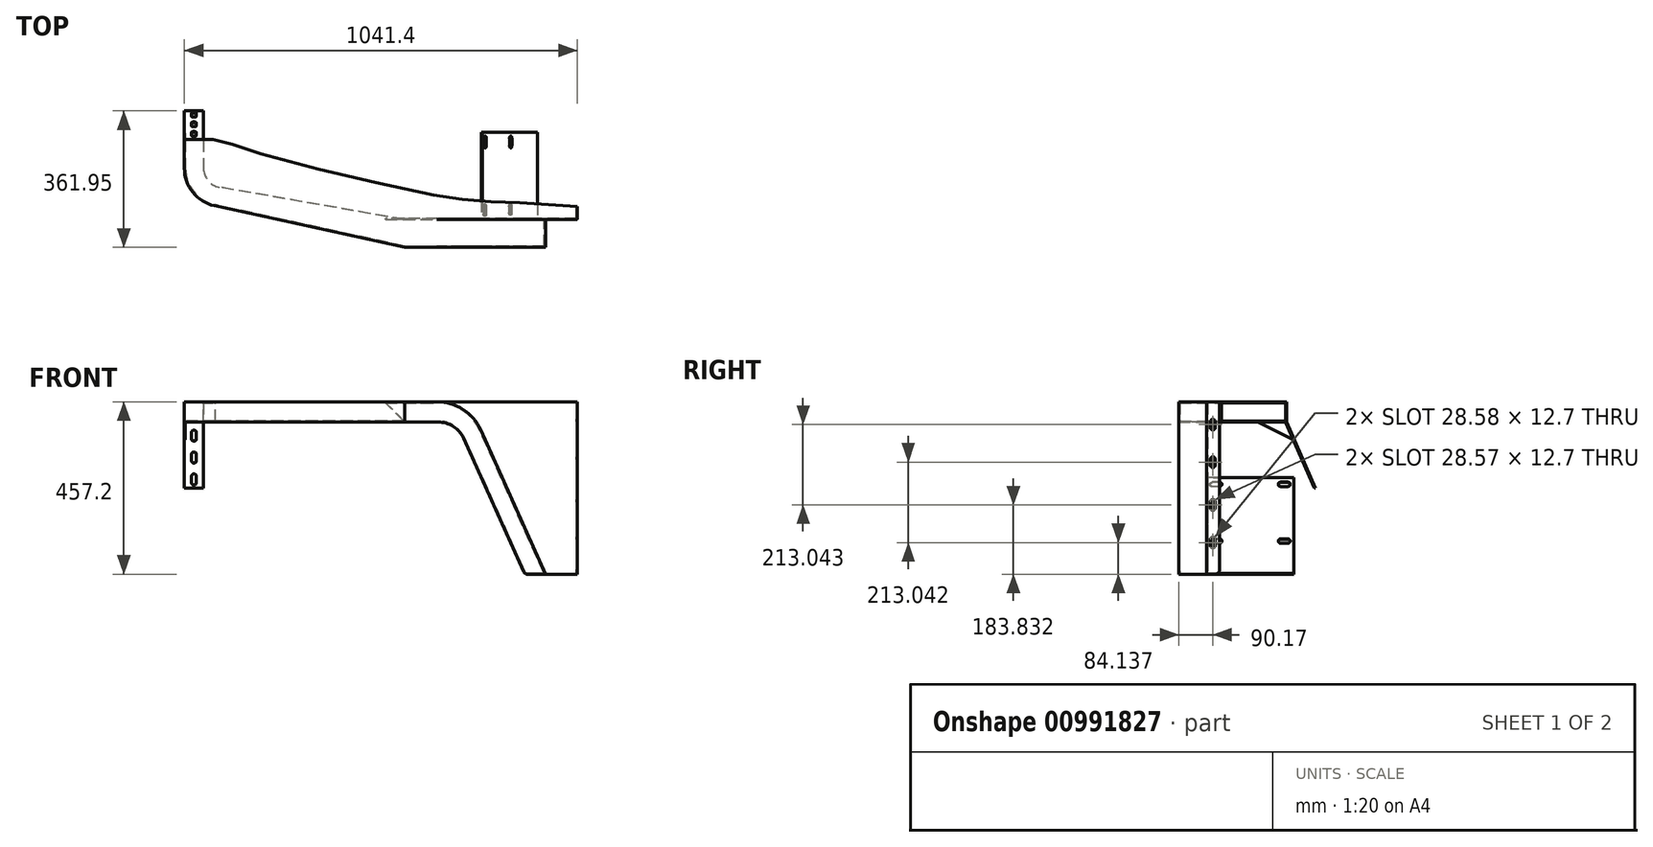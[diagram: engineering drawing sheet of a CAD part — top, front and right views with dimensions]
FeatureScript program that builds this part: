
annotation { "Feature Type Name" : "Feature", "Feature Type Description" : "" }
export const myFeature = defineFeature(function(context is Context, id is Id, definition is map)
    precondition{}
    {
        {
            var Q0;
            Q0=qCreatedBy(makeId("Top.planeOp"),FACE);
            var sketch = newSketch(context, id + "F0", { "sketchPlane" : qUnion([Q0])});
            skLineSegment(sketch, "E0", {"start": v(-1041.4, 177.8) * mm, "end": v(-965.2, 177.8) * mm});
            skLineSegment(sketch, "E1", {"start": v(0, 0) * mm, "end": v(-76.2, 5.08) * mm});
            skLineSegment(sketch, "E2", {"start": v(-76.2, 5.08) * mm, "end": v(-152.4, 10.16) * mm});
            skLineSegment(sketch, "E3", {"start": v(-152.4, 10.16) * mm, "end": v(-228.6, 12.7) * mm});
            skLineSegment(sketch, "E4", {"start": v(-228.6, 12.7) * mm, "end": v(-304.8, 19.05) * mm});
            skLineSegment(sketch, "E5", {"start": v(-304.8, 19.05) * mm, "end": v(-381, 30.48) * mm});
            skLineSegment(sketch, "E6", {"start": v(-381, 30.48) * mm, "end": v(-457.2, 46.99) * mm});
            skLineSegment(sketch, "E7", {"start": v(-457.2, 46.99) * mm, "end": v(-533.4, 63.5) * mm});
            skLineSegment(sketch, "E8", {"start": v(-533.4, 63.5) * mm, "end": v(-609.6, 81.73) * mm});
            skLineSegment(sketch, "E9", {"start": v(-609.6, 81.73) * mm, "end": v(-685.8, 99.57) * mm});
            skLineSegment(sketch, "E10", {"start": v(-685.8, 99.57) * mm, "end": v(-762, 119.38) * mm});
            skLineSegment(sketch, "E11", {"start": v(-762, 119.38) * mm, "end": v(-838.2, 139.7) * mm});
            skLineSegment(sketch, "E12", {"start": v(-838.2, 139.7) * mm, "end": v(-914.4, 165.1) * mm});
            skLineSegment(sketch, "E13", {"start": v(-914.4, 165.1) * mm, "end": v(-965.2, 177.8) * mm});
            skLineSegment(sketch, "E14", {"start": v(0, 0) * mm, "end": v(0, -31.75) * mm});
            skLineSegment(sketch, "E15", {"start": v(-1041.4, 177.8) * mm, "end": v(-1041.4, 101.6) * mm});
            skArc(sketch, "E16", {"start": v(-1041.4, 101.6) * mm, "mid": v(-1018.95, 37.9) * mm, "end": v(-961.5, 2.35) * mm});
            skLineSegment(sketch, "E17", {"start": v(0, -31.75) * mm, "end": v(-457.2, -31.75) * mm});
            skLineSegment(sketch, "E18", {"start": v(-457.2, -31.75) * mm, "end": v(-457.2, -107.95) * mm});
            skLineSegment(sketch, "E19", {"start": v(-961.5, 2.35) * mm, "end": v(-457.2, -107.95) * mm});
            skSolve(sketch);
        }
        {
            var Q0;
            Q0 = qSketchRegion(id + "F0", true);
            extrude(context, id + "F1", {"entities" : qUnion([Q0]), "oppositeDirection" : true, "depth" : 2.8 * mm, "offsetDistance" : 25.4 * mm});
        }
        {
            var Q0;
            Q0=makeQuery(id+"F1.opExtrude","SWEPT_FACE",FACE,{"disambiguationData":[OSD([sQuery(id+"F0.wireOp",EDGE,"E15")])]});
            var sketch = newSketch(context, id + "F2", { "sketchPlane" : qUnion([Q0])});
            skLineSegment(sketch, "E20", {"start": v(-177.8, -2.8) * mm, "end": v(-177.8, -53.33) * mm});
            skLineSegment(sketch, "E21", {"start": v(-177.9, -53.84) * mm, "end": v(-254, -228.2) * mm});
            skLineSegment(sketch, "E22", {"start": v(-254, -228.2) * mm, "end": v(-251.44, -229.3) * mm});
            skLineSegment(sketch, "E23", {"start": v(-251.44, -229.3) * mm, "end": v(-175.11, -54.42) * mm});
            skLineSegment(sketch, "E24", {"start": v(-175, -53.91) * mm, "end": v(-175, -2.8) * mm});
            skPoint(sketch, "E24.endSnap0", {"position": v(-139.7, -2.8) * mm});
            skLineSegment(sketch, "E25", {"start": v(-175, -2.8) * mm, "end": v(-177.8, -2.8) * mm});
            skPoint(sketch, "E26.visualSharp", {"position": v(-177.8, -53.6) * mm});
            skArc(sketch, "E26.filletArc", {"start": v(-177.9, -53.84) * mm, "mid": v(-177.83, -53.59) * mm, "end": v(-177.8, -53.33) * mm});
            skPoint(sketch, "E27.visualSharp", {"position": v(-175, -54.18) * mm});
            skArc(sketch, "E27.filletArc", {"start": v(-175.11, -54.42) * mm, "mid": v(-175.03, -54.17) * mm, "end": v(-175, -53.91) * mm});
            skSolve(sketch);
        }
        {
            var Q0;
            Q0 = qSketchRegion(id + "F2", true);
            extrude(context, id + "F3", {"entities" : qUnion([Q0]), "operationType" : NewBodyOperationType.ADD, "oppositeDirection" : true, "depth" : 50.8 * mm, "offsetDistance" : 25.4 * mm});
        }
        {
            var Q0;
            Q0=makeQuery(id+"F3.opExtrude","SWEPT_FACE",FACE,{"disambiguationData":[OSD([sQuery(id+"F2.wireOp",EDGE,"E21")])]});
            var sketch = newSketch(context, id + "F4", { "sketchPlane" : qUnion([Q0])});
            skArc(sketch, "E28", {"start": v(1022.34, -149.13) * mm, "mid": v(1015.88, -142.47) * mm, "end": v(1009.67, -149.36) * mm});
            skArc(sketch, "E29", {"start": v(1009.67, -167.32) * mm, "mid": v(1015.73, -174.2) * mm, "end": v(1022.35, -167.86) * mm});
            skArc(sketch, "E30", {"start": v(1022.35, -212) * mm, "mid": v(1016, -205.65) * mm, "end": v(1009.65, -212) * mm});
            skArc(sketch, "E31", {"start": v(1009.65, -231.36) * mm, "mid": v(1016, -237.71) * mm, "end": v(1022.35, -231.36) * mm});
            skArc(sketch, "E32", {"start": v(1022.35, -275.5) * mm, "mid": v(1015.84, -269.15) * mm, "end": v(1009.66, -275.81) * mm});
            skArc(sketch, "E33", {"start": v(1009.65, -294.86) * mm, "mid": v(1016, -301.21) * mm, "end": v(1022.35, -294.86) * mm});
            skLineSegment(sketch, "E34", {"start": v(1009.67, -148.27) * mm, "end": v(1009.67, -168.41) * mm});
            skLineSegment(sketch, "E35", {"start": v(1022.34, -148.5) * mm, "end": v(1022.35, -167.86) * mm});
            skLineSegment(sketch, "E36", {"start": v(1009.65, -212) * mm, "end": v(1009.65, -231.36) * mm});
            skLineSegment(sketch, "E37", {"start": v(1022.35, -212) * mm, "end": v(1022.35, -231.36) * mm});
            skLineSegment(sketch, "E38", {"start": v(1022.35, -275.5) * mm, "end": v(1022.35, -294.86) * mm});
            skLineSegment(sketch, "E39", {"start": v(1009.66, -275.81) * mm, "end": v(1009.65, -294.86) * mm});
            skSolve(sketch);
        }
        {
            var Q0;
            Q0 = qSketchRegion(id + "F4", true);
            extrude(context, id + "F5", {"entities" : qUnion([Q0]), "operationType" : NewBodyOperationType.REMOVE, "oppositeDirection" : true, "depth" : 25.4 * mm, "offsetDistance" : 25.4 * mm});
        }
        {
            var Q0;
            Q0=makeQuery(id+"F1.opExtrude","CAP_FACE",FACE,{"disambiguationData":[OSD([sQuery(id+"F0.wireOp",EDGE,"E0"),sQuery(id+"F0.wireOp",EDGE,"E1"),sQuery(id+"F0.wireOp",EDGE,"E2"),sQuery(id+"F0.wireOp",EDGE,"E3"),sQuery(id+"F0.wireOp",EDGE,"E4"),sQuery(id+"F0.wireOp",EDGE,"E5"),sQuery(id+"F0.wireOp",EDGE,"E6"),sQuery(id+"F0.wireOp",EDGE,"E7"),sQuery(id+"F0.wireOp",EDGE,"E8"),sQuery(id+"F0.wireOp",EDGE,"E9"),sQuery(id+"F0.wireOp",EDGE,"E10"),sQuery(id+"F0.wireOp",EDGE,"E11"),sQuery(id+"F0.wireOp",EDGE,"E12"),sQuery(id+"F0.wireOp",EDGE,"E13"),sQuery(id+"F0.wireOp",EDGE,"E14"),sQuery(id+"F0.wireOp",EDGE,"E15"),sQuery(id+"F0.wireOp",EDGE,"E16"),sQuery(id+"F0.wireOp",EDGE,"E17"),sQuery(id+"F0.wireOp",EDGE,"E18"),sQuery(id+"F0.wireOp",EDGE,"E19")])],"isStart":false});
            var sketch = newSketch(context, id + "F6", { "sketchPlane" : qUnion([Q0])});
            skLineSegment(sketch, "E40", {"start": v(-1041.4, -175) * mm, "end": v(-1041.4, -101.6) * mm});
            skLineSegment(sketch, "E41", {"start": v(-1038.6, -175) * mm, "end": v(-1038.6, -101.6) * mm});
            skArc(sketch, "E42", {"start": v(-961.5, -2.35) * mm, "mid": v(-1018.95, -37.9) * mm, "end": v(-1041.4, -101.6) * mm});
            skArc(sketch, "E43", {"start": v(-959.54, -4.79) * mm, "mid": v(-1016.33, -39.1) * mm, "end": v(-1038.6, -101.6) * mm});
            skLineSegment(sketch, "E44", {"start": v(-961.5, -2.35) * mm, "end": v(-457.2, 107.95) * mm});
            skLineSegment(sketch, "E45", {"start": v(-457.2, 105.08) * mm, "end": v(-959.54, -4.79) * mm});
            skLineSegment(sketch, "E46", {"start": v(-457.2, 105.08) * mm, "end": v(-457.2, 107.95) * mm});
            skLineSegment(sketch, "E47", {"start": v(-1041.4, -175) * mm, "end": v(-1038.6, -175) * mm});
            skSolve(sketch);
        }
        {
            var Q0;
            Q0 = qSketchRegion(id + "F6", true);
            extrude(context, id + "F7", {"entities" : qUnion([Q0]), "operationType" : NewBodyOperationType.ADD, "depth" : 50.8 * mm, "offsetDistance" : 25.4 * mm});
        }
        {
            var Q0;
            Q0=makeQuery(id+"F1.opExtrude","SWEPT_FACE",FACE,{"disambiguationData":[OSD([sQuery(id+"F0.wireOp",EDGE,"E17")])]});
            var sketch = newSketch(context, id + "F8", { "sketchPlane" : qUnion([Q0])});
            skLineSegment(sketch, "E48", {"start": v(0, 0) * mm, "end": v(0, -457.2) * mm});
            skLineSegment(sketch, "E49", {"start": v(0, -457.2) * mm, "end": v(-139.7, -457.2) * mm});
            skLineSegment(sketch, "E50", {"start": v(-457.2, 0) * mm, "end": v(-406.4, 0) * mm});
            skLineSegment(sketch, "E51", {"start": v(-457.2, 0) * mm, "end": v(-457.2, -2.8) * mm});
            skLineSegment(sketch, "E52", {"start": v(-406.4, 0) * mm, "end": v(0, 0) * mm});
            skPoint(sketch, "E53.visualSharp", {"position": v(-139.7, -457.2) * mm});
            skPoint(sketch, "E54.visualSharp", {"position": v(0, -457.2) * mm});
            skLineSegment(sketch, "E55", {"start": v(-139.7, -457.2) * mm, "end": v(-254, -203.2) * mm});
            skLineSegment(sketch, "E56", {"start": v(-457.2, -53.6) * mm, "end": v(-368.79, -53.6) * mm});
            skArc(sketch, "E57", {"start": v(-301.85, -96.88) * mm, "mid": v(-328.93, -65.36) * mm, "end": v(-368.79, -53.6) * mm});
            skLineSegment(sketch, "E58", {"start": v(-254, -203.2) * mm, "end": v(-301.85, -96.88) * mm});
            skLineSegment(sketch, "E59", {"start": v(-457.2, -53.6) * mm, "end": v(-508, -2.8) * mm});
            skLineSegment(sketch, "E60", {"start": v(-508, -2.8) * mm, "end": v(-457.2, -2.8) * mm});
            skSolve(sketch);
        }
        {
            var Q0;
            Q0 = qSketchRegion(id + "F8", true);
            extrude(context, id + "F9", {"entities" : qUnion([Q0]), "operationType" : NewBodyOperationType.ADD, "depth" : 2.8 * mm, "offsetDistance" : 25.4 * mm});
        }
        {
            var Q0;
            Q0=makeQuery(id+"F7.boolean.opBoolean","MERGE",FACE,{"derivedFrom":[makeQuery(id+"F3.boolean.opBoolean","MERGE",FACE,{"derivedFrom":[makeQuery(id+"F1.opExtrude","SWEPT_FACE",FACE,{"disambiguationData":[OSD([sQuery(id+"F0.wireOp",EDGE,"E15")])]}),makeQuery(id+"F3.opExtrude","CAP_FACE",FACE,{"disambiguationData":[OSD([sQuery(id+"F2.wireOp",EDGE,"E20"),sQuery(id+"F2.wireOp",EDGE,"E21"),sQuery(id+"F2.wireOp",EDGE,"E22"),sQuery(id+"F2.wireOp",EDGE,"E23"),sQuery(id+"F2.wireOp",EDGE,"E24"),sQuery(id+"F2.wireOp",EDGE,"E25"),sQuery(id+"F2.wireOp",EDGE,"E26.filletArc"),sQuery(id+"F2.wireOp",EDGE,"E27.filletArc")])],"isStart":true})]}),makeQuery(id+"F7.opExtrude","SWEPT_FACE",FACE,{"disambiguationData":[OSD([sQuery(id+"F6.wireOp",EDGE,"E40")])]})]});
            var sketch = newSketch(context, id + "F10", { "sketchPlane" : qUnion([Q0])});
            skLineSegment(sketch, "E61", {"start": v(-101.6, -53.6) * mm, "end": v(-195.23, -100.51) * mm});
            skLineSegment(sketch, "E62", {"start": v(-195.23, -100.51) * mm, "end": v(-175, -53.91) * mm});
            skLineSegment(sketch, "E63", {"start": v(-175, -53.6) * mm, "end": v(-101.6, -53.6) * mm});
            skSolve(sketch);
        }
        {
            var Q0;
            {var subQ1=sQuery(id+"F10.wireOp",EDGE,"E61");Q0=makeQuery(id+"F10.imprint","IMPRINT",FACE,{"disambiguationData":[TD([[makeQuery(id+"F10.imprint","IMPRINT",EDGE,{"derivedFrom":subQ1}),-1.0]])]});}
            extrude(context, id + "F11", {"entities" : qUnion([Q0]), "operationType" : NewBodyOperationType.ADD, "oppositeDirection" : true, "depth" : 2.8 * mm, "offsetDistance" : 25.4 * mm});
        }
        {
            var Q0;
            Q0=makeQuery(id+"F9.opExtrude","SWEPT_EDGE",EDGE,{"disambiguationData":[OSD([sQuery(id+"F8.wireOp",EDGE,"E49"),sQuery(id+"F8.wireOp",EDGE,"E55")])]});
            fillet(context, id + "F12", {"entities" : qUnion([Q0]), "radius" : 12.7 * mm, "tangentPropagation" : true, "allowEdgeOverflow" : false});
        }
        {
            var Q0;
            Q0=makeQuery(id+"F9.opExtrude","CAP_FACE",FACE,{"disambiguationData":[OSD([sQuery(id+"F8.wireOp",EDGE,"E48"),sQuery(id+"F8.wireOp",EDGE,"E49"),sQuery(id+"F8.wireOp",EDGE,"E50"),sQuery(id+"F8.wireOp",EDGE,"E51"),sQuery(id+"F8.wireOp",EDGE,"E52"),sQuery(id+"F8.wireOp",EDGE,"E55"),sQuery(id+"F8.wireOp",EDGE,"E56"),sQuery(id+"F8.wireOp",EDGE,"E57"),sQuery(id+"F8.wireOp",EDGE,"E58"),sQuery(id+"F8.wireOp",EDGE,"E59"),sQuery(id+"F8.wireOp",EDGE,"E60")])],"isStart":false});
            var sketch = newSketch(context, id + "F13", { "sketchPlane" : qUnion([Q0])});
            skLineSegment(sketch, "E64", {"start": v(-457.2, 0) * mm, "end": v(-371.85, 0) * mm});
            skLineSegment(sketch, "E65", {"start": v(-457.2, 0) * mm, "end": v(-457.2, -2.8) * mm});
            skLineSegment(sketch, "E66", {"start": v(-457.2, -2.8) * mm, "end": v(-371.85, -2.8) * mm});
            skLineSegment(sketch, "E67", {"start": v(-84, -457.2) * mm, "end": v(-256.04, -74.88) * mm});
            skArc(sketch, "E68", {"start": v(-256.04, -74.88) * mm, "mid": v(-302.9, -20.35) * mm, "end": v(-371.85, 0) * mm});
            skArc(sketch, "E69", {"start": v(-258.58, -76.03) * mm, "mid": v(-304.4, -22.7) * mm, "end": v(-371.85, -2.8) * mm});
            skLineSegment(sketch, "E70", {"start": v(-87.06, -457.2) * mm, "end": v(-258.58, -76.03) * mm});
            skLineSegment(sketch, "E71", {"start": v(-84, -457.2) * mm, "end": v(-87.06, -457.2) * mm});
            skSolve(sketch);
        }
        {
            var Q0;
            Q0 = qSketchRegion(id + "F10", true);
            var Q1;
            Q1 = qSketchRegion(id + "F13", true);
            extrude(context, id + "F14", {"entities" : qUnion([Q0, Q1]), "operationType" : NewBodyOperationType.ADD, "depth" : 76.2 * mm - 2.8 * mm, "offsetDistance" : 25.4 * mm});
        }
        {
            var Q0;
            Q0=makeQuery(id+"F14.opExtrude","CAP_FACE",FACE,{"disambiguationData":[OSD([sQuery(id+"F13.wireOp",EDGE,"E64"),sQuery(id+"F13.wireOp",EDGE,"E65"),sQuery(id+"F13.wireOp",EDGE,"E66"),sQuery(id+"F13.wireOp",EDGE,"E67"),sQuery(id+"F13.wireOp",EDGE,"E68"),sQuery(id+"F13.wireOp",EDGE,"E69"),sQuery(id+"F13.wireOp",EDGE,"E70"),sQuery(id+"F13.wireOp",EDGE,"E71")])],"isStart":false});
            var sketch = newSketch(context, id + "F15", { "sketchPlane" : qUnion([Q0])});
            skLineSegment(sketch, "E72", {"start": v(-457.2, -2.8) * mm, "end": v(-457.2, -53.6) * mm});
            skLineSegment(sketch, "E73", {"start": v(-457.2, -2.8) * mm, "end": v(-371.85, -2.8) * mm});
            skArc(sketch, "E74", {"start": v(-258.58, -76.03) * mm, "mid": v(-304.4, -22.7) * mm, "end": v(-371.85, -2.8) * mm});
            skLineSegment(sketch, "E75", {"start": v(-87.06, -457.2) * mm, "end": v(-258.58, -76.03) * mm});
            skLineSegment(sketch, "E76", {"start": v(-457.2, -53.6) * mm, "end": v(-368.79, -53.6) * mm});
            skArc(sketch, "E77", {"start": v(-301.85, -96.88) * mm, "mid": v(-328.93, -65.36) * mm, "end": v(-368.79, -53.6) * mm});
            skLineSegment(sketch, "E78", {"start": v(-143.07, -449.71) * mm, "end": v(-301.85, -96.88) * mm});
            skLineSegment(sketch, "E79", {"start": v(-131.49, -457.2) * mm, "end": v(-87.06, -457.2) * mm});
            skPoint(sketch, "E80.visualSharp", {"position": v(-139.7, -457.2) * mm});
            skArc(sketch, "E80.filletArc", {"start": v(-143.07, -449.71) * mm, "mid": v(-138.38, -455.16) * mm, "end": v(-131.49, -457.2) * mm});
            skSolve(sketch);
        }
        {
            var Q0;
            Q0=makeQuery(id+"F15.imprint","IMPRINT",FACE,{"disambiguationData":[TD([[makeQuery(id+"F15.imprint","IMPRINT",EDGE,{"derivedFrom":sQuery(id+"F15.wireOp",EDGE,"E72")}),1.0]])]});
            extrude(context, id + "F16", {"entities" : qUnion([Q0]), "operationType" : NewBodyOperationType.ADD, "oppositeDirection" : true, "depth" : 2.8 * mm, "offsetDistance" : 25.4 * mm});
        }
        {
            var Q0;
            Q0=makeQuery(id+"F16.boolean.opBoolean","MERGE",FACE,{"derivedFrom":[makeQuery(id+"F7.opExtrude","CAP_FACE",FACE,{"disambiguationData":[OSD([sQuery(id+"F6.wireOp",EDGE,"E40"),sQuery(id+"F6.wireOp",EDGE,"E41"),sQuery(id+"F6.wireOp",EDGE,"E42"),sQuery(id+"F6.wireOp",EDGE,"E43"),sQuery(id+"F6.wireOp",EDGE,"E44"),sQuery(id+"F6.wireOp",EDGE,"E45"),sQuery(id+"F6.wireOp",EDGE,"E46"),sQuery(id+"F6.wireOp",EDGE,"E47")])],"isStart":false}),makeQuery(id+"F16.opExtrude","SWEPT_FACE",FACE,{"disambiguationData":[OSD([sQuery(id+"F15.wireOp",EDGE,"E76")])]})]});
            var sketch = newSketch(context, id + "F17", { "sketchPlane" : qUnion([Q0])});
            skLineSegment(sketch, "E81", {"start": v(-1038.6, -101.6) * mm, "end": v(-1038.6, -175) * mm});
            skArc(sketch, "E82", {"start": v(-959.54, -4.79) * mm, "mid": v(-1016.33, -39.1) * mm, "end": v(-1038.6, -101.6) * mm});
            skLineSegment(sketch, "E83", {"start": v(-419.1, 105.16) * mm, "end": v(-419.1, 34.54) * mm});
            skLineSegment(sketch, "E84", {"start": v(-419.1, 34.54) * mm, "end": v(-457.2, 34.54) * mm});
            skLineSegment(sketch, "E85", {"start": v(-1038.6, -175) * mm, "end": v(-990.6, -175) * mm});
            skLineSegment(sketch, "E86", {"start": v(-990.6, -175) * mm, "end": v(-990.6, -101.6) * mm});
            skArc(sketch, "E87", {"start": v(-948.57, -51.56) * mm, "mid": v(-978.7, -68.93) * mm, "end": v(-990.6, -101.6) * mm});
            skLineSegment(sketch, "E88", {"start": v(-457.2, 34.54) * mm, "end": v(-948.57, -51.56) * mm});
            skLineSegment(sketch, "E89", {"start": v(-419.1, 105.16) * mm, "end": v(-457.2, 105.16) * mm});
            skLineSegment(sketch, "E90", {"start": v(-457.2, 105.16) * mm, "end": v(-959.54, -4.79) * mm});
            skSolve(sketch);
        }
        {
            var Q0;
            {var subQ0=sQuery(id+"F8.wireOp",EDGE,"E55");var subQ1=sQuery(id+"F8.wireOp",EDGE,"E49");var subQ2=sQuery(id+"F8.wireOp",EDGE,"E57");var subQ3=sQuery(id+"F8.wireOp",EDGE,"E59");var subQ4=sQuery(id+"F8.wireOp",EDGE,"E58");var subQ5=sQuery(id+"F8.wireOp",EDGE,"E56");Q0=makeQuery(id+"F14.boolean.opBoolean","SPLIT",FACE,{"disambiguationData":[TD([makeQuery(id+"F9.opExtrude","SWEPT_FACE",FACE,{"disambiguationData":[OSD([subQ5])]})])],"derivedFrom":makeQuery(id+"F9.opExtrude","CAP_FACE",FACE,{"disambiguationData":[OSD([sQuery(id+"F8.wireOp",EDGE,"E48"),subQ1,sQuery(id+"F8.wireOp",EDGE,"E50"),sQuery(id+"F8.wireOp",EDGE,"E51"),sQuery(id+"F8.wireOp",EDGE,"E52"),subQ0,subQ5,subQ2,subQ4,subQ3,sQuery(id+"F8.wireOp",EDGE,"E60")])],"isStart":false})});}
            var sketch = newSketch(context, id + "F18", { "sketchPlane" : qUnion([Q0])});
            skLineSegment(sketch, "E91", {"start": v(-87.06, -457.2) * mm, "end": v(-88.31, -454.4) * mm});
            skLineSegment(sketch, "E92", {"start": v(-88.31, -454.4) * mm, "end": v(-131.49, -454.4) * mm});
            skLineSegment(sketch, "E93", {"start": v(-419.1, -50.8) * mm, "end": v(-368.79, -50.8) * mm});
            skLineSegment(sketch, "E94", {"start": v(-419.1, -53.6) * mm, "end": v(-368.79, -53.6) * mm});
            skArc(sketch, "E95", {"start": v(-301.85, -96.88) * mm, "mid": v(-328.93, -65.36) * mm, "end": v(-368.79, -53.6) * mm});
            skLineSegment(sketch, "E96", {"start": v(-301.85, -96.88) * mm, "end": v(-143.07, -449.71) * mm});
            skArc(sketch, "E97", {"start": v(-143.07, -449.71) * mm, "mid": v(-138.38, -455.16) * mm, "end": v(-131.49, -457.2) * mm});
            skLineSegment(sketch, "E98", {"start": v(-87.06, -457.2) * mm, "end": v(-131.49, -457.2) * mm});
            skArc(sketch, "E99", {"start": v(-140.52, -448.57) * mm, "mid": v(-136.87, -452.82) * mm, "end": v(-131.49, -454.4) * mm});
            skArc(sketch, "E100", {"start": v(-299.3, -95.73) * mm, "mid": v(-327.41, -63.01) * mm, "end": v(-368.79, -50.8) * mm});
            skLineSegment(sketch, "E101", {"start": v(-140.52, -448.57) * mm, "end": v(-299.3, -95.73) * mm});
            skLineSegment(sketch, "E102", {"start": v(-419.1, -50.8) * mm, "end": v(-419.1, -53.6) * mm});
            skSolve(sketch);
        }
        {
            var Q0;
            Q0 = qSketchRegion(id + "F18", true);
            var Q1;
            Q1=makeQuery(id+"F16.opExtrude","CAP_FACE",FACE,{"disambiguationData":[OSD([sQuery(id+"F15.wireOp",EDGE,"E72"),sQuery(id+"F15.wireOp",EDGE,"E73"),sQuery(id+"F15.wireOp",EDGE,"E74"),sQuery(id+"F15.wireOp",EDGE,"E75"),sQuery(id+"F15.wireOp",EDGE,"E76"),sQuery(id+"F15.wireOp",EDGE,"E77"),sQuery(id+"F15.wireOp",EDGE,"E78"),sQuery(id+"F15.wireOp",EDGE,"E79"),sQuery(id+"F15.wireOp",EDGE,"E80.filletArc")])],"isStart":false});
            extrude(context, id + "F19", {"entities" : qUnion([Q0]), "operationType" : NewBodyOperationType.ADD, "endBound" : BoundingType.UP_TO_SURFACE, "depth" : 25.4 * mm, "endBoundEntityFace" : qUnion([Q1]), "offsetDistance" : 25.4 * mm});
        }
        {
            var Q0;
            Q0=makeQuery(id+"F17.imprint","IMPRINT",FACE,{"disambiguationData":[TD([[makeQuery(id+"F17.imprint","IMPRINT",EDGE,{"derivedFrom":sQuery(id+"F17.wireOp",EDGE,"E81")}),1.0]])]});
            extrude(context, id + "F20", {"entities" : qUnion([Q0]), "operationType" : NewBodyOperationType.ADD, "oppositeDirection" : true, "depth" : 2.8 * mm, "offsetDistance" : 25.4 * mm});
        }
        {
            var Q0;
            Q0=makeQuery(id+"F9.boolean.opBoolean","MERGE",FACE,{"derivedFrom":[makeQuery(id+"F1.opExtrude","SWEPT_FACE",FACE,{"disambiguationData":[OSD([sQuery(id+"F0.wireOp",EDGE,"E14")])]}),makeQuery(id+"F9.opExtrude","SWEPT_FACE",FACE,{"disambiguationData":[OSD([sQuery(id+"F8.wireOp",EDGE,"E48")])]})]});
            var sketch = newSketch(context, id + "F21", { "sketchPlane" : qUnion([Q0])});
            skLineSegment(sketch, "E103.bottom", {"start": v(-31.75, -2.8) * mm, "end": v(0, -2.8) * mm});
            skLineSegment(sketch, "E103.top", {"start": v(-31.75, -457.2) * mm, "end": v(-12.7, -457.2) * mm});
            skLineSegment(sketch, "E103.left", {"start": v(-31.75, -2.8) * mm, "end": v(-31.75, -457.2) * mm});
            skLineSegment(sketch, "E103.right", {"start": v(0, -2.8) * mm, "end": v(0, -444.5) * mm});
            skArc(sketch, "E104", {"start": v(-11.43, -52.39) * mm, "mid": v(-17.78, -46.04) * mm, "end": v(-24.13, -52.39) * mm});
            skArc(sketch, "E105", {"start": v(-24.13, -68.26) * mm, "mid": v(-17.78, -74.61) * mm, "end": v(-11.43, -68.26) * mm});
            skLineSegment(sketch, "E106", {"start": v(-11.43, -52.39) * mm, "end": v(-11.43, -68.26) * mm});
            skLineSegment(sketch, "E107", {"start": v(-24.13, -52.39) * mm, "end": v(-24.13, -68.26) * mm});
            skArc(sketch, "E108", {"start": v(-24.13, -381) * mm, "mid": v(-17.78, -387.35) * mm, "end": v(-11.43, -381) * mm});
            skArc(sketch, "E109", {"start": v(-11.43, -365.12) * mm, "mid": v(-17.78, -358.77) * mm, "end": v(-24.13, -365.12) * mm});
            skLineSegment(sketch, "E110", {"start": v(-11.43, -365.12) * mm, "end": v(-11.43, -381) * mm});
            skLineSegment(sketch, "E111", {"start": v(-24.13, -365.12) * mm, "end": v(-24.13, -381) * mm});
            skArc(sketch, "E112", {"start": v(-11.43, -152.08) * mm, "mid": v(-17.78, -145.73) * mm, "end": v(-24.13, -152.08) * mm});
            skArc(sketch, "E113", {"start": v(-24.13, -167.96) * mm, "mid": v(-17.78, -174.3) * mm, "end": v(-11.43, -167.96) * mm});
            skLineSegment(sketch, "E114", {"start": v(-24.13, -152.08) * mm, "end": v(-24.13, -167.96) * mm});
            skLineSegment(sketch, "E115", {"start": v(-11.43, -167.96) * mm, "end": v(-11.43, -152.08) * mm});
            skArc(sketch, "E116", {"start": v(-11.43, -265.43) * mm, "mid": v(-17.78, -259.08) * mm, "end": v(-24.13, -265.43) * mm});
            skArc(sketch, "E117", {"start": v(-24.13, -281.3) * mm, "mid": v(-17.78, -287.65) * mm, "end": v(-11.43, -281.3) * mm});
            skLineSegment(sketch, "E118", {"start": v(-24.13, -265.43) * mm, "end": v(-24.13, -281.3) * mm});
            skLineSegment(sketch, "E119", {"start": v(-11.43, -265.43) * mm, "end": v(-11.43, -281.3) * mm});
            skPoint(sketch, "E120.visualSharp", {"position": v(0, -457.2) * mm});
            skArc(sketch, "E120.filletArc", {"start": v(-12.7, -457.2) * mm, "mid": v(-3.72, -453.48) * mm, "end": v(0, -444.5) * mm});
            skSolve(sketch);
        }
        {
            var Q0;
            Q0 = qSketchRegion(id + "F21", true);
            extrude(context, id + "F22", {"entities" : qUnion([Q0]), "operationType" : NewBodyOperationType.ADD, "oppositeDirection" : true, "depth" : 2.8 * mm, "offsetDistance" : 25.4 * mm});
        }
        {
            var Q0;
            Q0=makeQuery(id+"F9.opExtrude","CAP_FACE",FACE,{"disambiguationData":[OSD([sQuery(id+"F8.wireOp",EDGE,"E48"),sQuery(id+"F8.wireOp",EDGE,"E49"),sQuery(id+"F8.wireOp",EDGE,"E50"),sQuery(id+"F8.wireOp",EDGE,"E51"),sQuery(id+"F8.wireOp",EDGE,"E52"),sQuery(id+"F8.wireOp",EDGE,"E55"),sQuery(id+"F8.wireOp",EDGE,"E56"),sQuery(id+"F8.wireOp",EDGE,"E57"),sQuery(id+"F8.wireOp",EDGE,"E58"),sQuery(id+"F8.wireOp",EDGE,"E59"),sQuery(id+"F8.wireOp",EDGE,"E60")])],"isStart":true});
            var sketch = newSketch(context, id + "F23", { "sketchPlane" : qUnion([Q0])});
            skPoint(sketch, "E121", {"position": v(138.38, -455.16) * mm});
            skLineSegment(sketch, "E122", {"start": v(131.49, -457.2) * mm, "end": v(106.09, -457.2) * mm});
            skLineSegment(sketch, "E123", {"start": v(143.07, -449.71) * mm, "end": v(254.36, -202.4) * mm});
            skArc(sketch, "E124", {"start": v(131.49, -457.2) * mm, "mid": v(138.38, -455.16) * mm, "end": v(143.07, -449.71) * mm});
            skLineSegment(sketch, "E125", {"start": v(106.09, -457.2) * mm, "end": v(106.09, -454.4) * mm});
            skLineSegment(sketch, "E126", {"start": v(106.09, -454.4) * mm, "end": v(131.49, -454.4) * mm});
            skArc(sketch, "E127", {"start": v(131.49, -454.4) * mm, "mid": v(136.87, -452.82) * mm, "end": v(140.52, -448.57) * mm});
            skLineSegment(sketch, "E128", {"start": v(254.36, -202.4) * mm, "end": v(251.8, -201.26) * mm});
            skLineSegment(sketch, "E129", {"start": v(251.8, -201.26) * mm, "end": v(140.52, -448.57) * mm});
            skSolve(sketch);
        }
        {
            var Q0;
            Q0 = qSketchRegion(id + "F23", true);
            extrude(context, id + "F24", {"entities" : qUnion([Q0]), "operationType" : NewBodyOperationType.ADD, "depth" : 228.6 * mm, "offsetDistance" : 25.4 * mm});
        }
        {
            var Q0;
            Q0=makeQuery(id+"F24.boolean.opBoolean","MERGE",FACE,{"derivedFrom":[makeQuery(id+"F19.boolean.opBoolean","MERGE",FACE,{"derivedFrom":[makeQuery(id+"F9.opExtrude","SWEPT_FACE",FACE,{"disambiguationData":[OSD([sQuery(id+"F8.wireOp",EDGE,"E55"),sQuery(id+"F8.wireOp",EDGE,"E58")])]}),makeQuery(id+"F16.opExtrude","SWEPT_FACE",FACE,{"disambiguationData":[OSD([sQuery(id+"F15.wireOp",EDGE,"E78")])]}),makeQuery(id+"F19.opExtrude","SWEPT_FACE",FACE,{"disambiguationData":[OSD([sQuery(id+"F18.wireOp",EDGE,"E96")])]})]}),makeQuery(id+"F24.opExtrude","SWEPT_FACE",FACE,{"disambiguationData":[OSD([sQuery(id+"F23.wireOp",EDGE,"E123")])]})]});
            var sketch = newSketch(context, id + "F25", { "sketchPlane" : qUnion([Q0])});
            skArc(sketch, "E130", {"start": v(-161.93, -105.6) * mm, "mid": v(-155.58, -99.25) * mm, "end": v(-161.93, -92.9) * mm});
            skArc(sketch, "E131", {"start": v(-180.98, -92.9) * mm, "mid": v(-187.33, -99.25) * mm, "end": v(-180.98, -105.6) * mm});
            skArc(sketch, "E132", {"start": v(-180.97, -258) * mm, "mid": v(-187.32, -264.35) * mm, "end": v(-180.97, -270.7) * mm});
            skArc(sketch, "E133", {"start": v(-161.92, -270.7) * mm, "mid": v(-155.57, -264.35) * mm, "end": v(-161.92, -258) * mm});
            skArc(sketch, "E134", {"start": v(0, -92.9) * mm, "mid": v(-6.35, -99.25) * mm, "end": v(0, -105.6) * mm});
            skArc(sketch, "E135", {"start": v(19.05, -105.6) * mm, "mid": v(25.4, -99.25) * mm, "end": v(19.05, -92.9) * mm});
            skArc(sketch, "E136", {"start": v(0, -258) * mm, "mid": v(-6.35, -264.35) * mm, "end": v(0, -270.7) * mm});
            skLineSegment(sketch, "E137", {"start": v(-180.98, -105.6) * mm, "end": v(-161.93, -105.6) * mm});
            skLineSegment(sketch, "E138", {"start": v(-180.98, -92.9) * mm, "end": v(-161.93, -92.9) * mm});
            skLineSegment(sketch, "E139", {"start": v(0, -92.9) * mm, "end": v(19.05, -92.9) * mm});
            skLineSegment(sketch, "E140", {"start": v(0, -105.6) * mm, "end": v(19.05, -105.6) * mm});
            skLineSegment(sketch, "E141", {"start": v(-180.97, -258) * mm, "end": v(-161.92, -258) * mm});
            skLineSegment(sketch, "E142", {"start": v(-161.92, -270.7) * mm, "end": v(-180.97, -270.7) * mm});
            skLineSegment(sketch, "E143", {"start": v(0, -258) * mm, "end": v(15.88, -258) * mm});
            skLineSegment(sketch, "E144", {"start": v(15.88, -270.7) * mm, "end": v(0, -270.7) * mm});
            skArc(sketch, "E145", {"start": v(15.88, -270.7) * mm, "mid": v(22.23, -264.35) * mm, "end": v(15.88, -258) * mm});
            skSolve(sketch);
        }
        {
            var Q0;
            Q0 = qSketchRegion(id + "F25", true);
            extrude(context, id + "F26", {"entities" : qUnion([Q0]), "operationType" : NewBodyOperationType.REMOVE, "oppositeDirection" : true, "depth" : 25.4 * mm, "offsetDistance" : 25.4 * mm});
        }
        {
            var Q0;
            Q0=makeQuery(id+"F9.opExtrude","CAP_EDGE",EDGE,{"disambiguationData":[OSD([sQuery(id+"F8.wireOp",EDGE,"E48")])],"isStart":false});
            fillet(context, id + "F27", {"entities" : qUnion([Q0]), "radius" : 2.54 * mm, "tangentPropagation" : true, "allowEdgeOverflow" : false});
        }
    });
